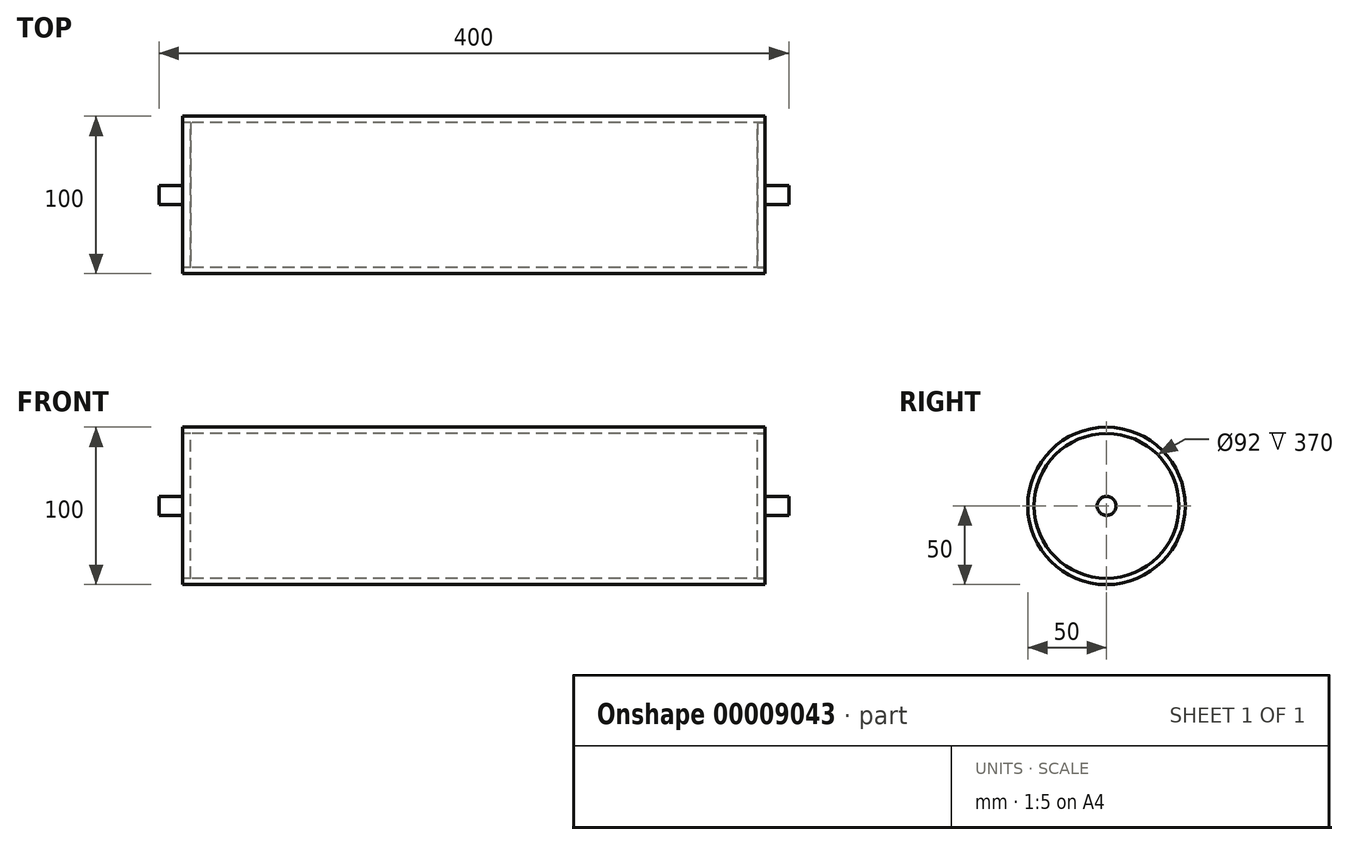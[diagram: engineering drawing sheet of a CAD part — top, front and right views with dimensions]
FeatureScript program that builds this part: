
annotation { "Feature Type Name" : "Feature", "Feature Type Description" : "" }
export const myFeature = defineFeature(function(context is Context, id is Id, definition is map)
    precondition{}
    {
        {
            var Q0;
            Q0=qCreatedBy(makeId("Right.planeOp"),FACE);
            var sketch = newSketch(context, id + "F0", { "sketchPlane" : qUnion([Q0])});
            skCircle(sketch, "E0", {"center": v(0, 0) * mm, "radius": 46 * mm});
            skCircle(sketch, "E1", {"center": v(0, 0) * mm, "radius": 50 * mm});
            skSolve(sketch);
        }
        {
            var Q0;
            Q0 = qSketchRegion(id + "F0", true);
            extrude(context, id + "F1", {"entities" : qUnion([Q0]), "depth" : 370 * mm});
        }
        {
            var Q0;
            Q0=makeQuery(id+"F1.opExtrude","CAP_FACE",FACE,{"disambiguationData":[OSD([sQuery(id+"F0.wireOp",EDGE,"E0"),sQuery(id+"F0.wireOp",EDGE,"E1")])],"isStart":true});
            var sketch = newSketch(context, id + "F2", { "sketchPlane" : qUnion([Q0])});
            skCircle(sketch, "E2", {"center": v(0, 0) * mm, "radius": 46 * mm});
            skSolve(sketch);
        }
        {
            var Q0;
            Q0 = qSketchRegion(id + "F2", true);
            extrude(context, id + "F3", {"entities" : qUnion([Q0]), "oppositeDirection" : true, "depth" : 5 * mm});
        }
        {
            var Q0;
            Q0=makeQuery(id+"F3.opExtrude","CAP_FACE",FACE,{"disambiguationData":[OSD([sQuery(id+"F2.wireOp",EDGE,"E2")])],"isStart":true});
            var sketch = newSketch(context, id + "F4", { "sketchPlane" : qUnion([Q0])});
            skCircle(sketch, "E3", {"center": v(0, 0) * mm, "radius": 6 * mm});
            skSolve(sketch);
        }
        {
            var Q0;
            Q0 = qSketchRegion(id + "F4", true);
            extrude(context, id + "F5", {"entities" : qUnion([Q0]), "operationType" : NewBodyOperationType.ADD, "depth" : 15 * mm});
        }
        {
            var Q0;
            Q0=makeQuery(id+"F1.opExtrude","CAP_FACE",FACE,{"disambiguationData":[OSD([sQuery(id+"F0.wireOp",EDGE,"E0"),sQuery(id+"F0.wireOp",EDGE,"E1")])],"isStart":false});
            var sketch = newSketch(context, id + "F6", { "sketchPlane" : qUnion([Q0])});
            skCircle(sketch, "E4", {"center": v(0, 0) * mm, "radius": 46 * mm});
            skSolve(sketch);
        }
        {
            var Q0;
            Q0 = qSketchRegion(id + "F6", true);
            extrude(context, id + "F7", {"entities" : qUnion([Q0]), "oppositeDirection" : true, "depth" : 5 * mm});
        }
        {
            var Q0;
            Q0=makeQuery(id+"F7.opExtrude","CAP_FACE",FACE,{"disambiguationData":[OSD([sQuery(id+"F6.wireOp",EDGE,"E4")])],"isStart":true});
            var sketch = newSketch(context, id + "F8", { "sketchPlane" : qUnion([Q0])});
            skCircle(sketch, "E5", {"center": v(0, 0) * mm, "radius": 6 * mm});
            skSolve(sketch);
        }
        {
            var Q0;
            Q0 = qSketchRegion(id + "F8", true);
            extrude(context, id + "F9", {"entities" : qUnion([Q0]), "operationType" : NewBodyOperationType.ADD, "depth" : 15 * mm});
        }
    });
